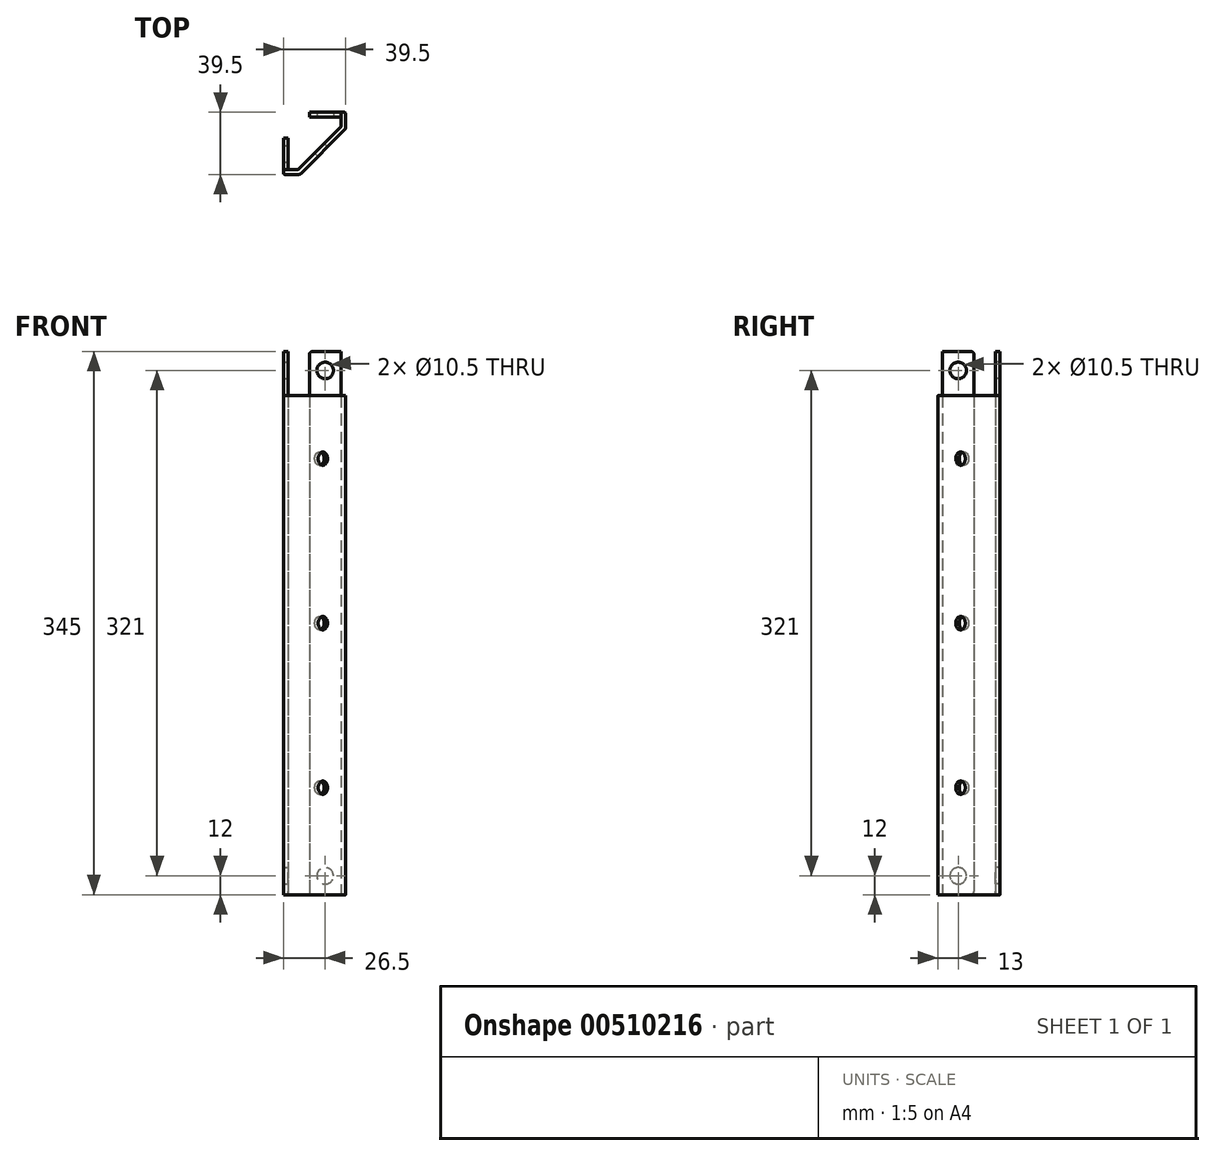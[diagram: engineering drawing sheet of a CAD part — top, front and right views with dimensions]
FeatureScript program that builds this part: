
annotation { "Feature Type Name" : "Feature", "Feature Type Description" : "" }
export const myFeature = defineFeature(function(context is Context, id is Id, definition is map)
    precondition{}
    {
        {
            var Q0;
            Q0=qCreatedBy(makeId("Top.planeOp"),FACE);
            var sketch = newSketch(context, id + "F0", { "sketchPlane" : qUnion([Q0])});
            skLineSegment(sketch, "E0", {"start": v(0, 53.87) * mm, "end": v(0, -58.58) * mm, "construction": true});
            skLineSegment(sketch, "E1", {"start": v(-55.23, 0) * mm, "end": v(53.75, 0) * mm, "construction": true});
            skLineSegment(sketch, "E2.bottom", {"start": v(-19.75, 19.75) * mm, "end": v(19.75, 19.75) * mm, "construction": true});
            skLineSegment(sketch, "E2.top", {"start": v(-19.75, -19.75) * mm, "end": v(19.75, -19.75) * mm, "construction": true});
            skLineSegment(sketch, "E2.left", {"start": v(-19.75, 19.75) * mm, "end": v(-19.75, -19.75) * mm, "construction": true});
            skLineSegment(sketch, "E2.right", {"start": v(19.75, 19.75) * mm, "end": v(19.75, -19.75) * mm, "construction": true});
            skLineSegment(sketch, "E3", {"start": v(-19.75, -19.75) * mm, "end": v(-19.75, 3.25) * mm});
            skLineSegment(sketch, "E4", {"start": v(-19.75, 3.25) * mm, "end": v(-16.75, 3.25) * mm});
            skLineSegment(sketch, "E5", {"start": v(-16.75, 3.25) * mm, "end": v(-16.75, -16.75) * mm});
            skLineSegment(sketch, "E6", {"start": v(-19.75, -19.75) * mm, "end": v(-9.25, -19.75) * mm});
            skLineSegment(sketch, "E7", {"start": v(-9.25, -19.75) * mm, "end": v(19.75, 9.25) * mm, "construction": true});
            skLineSegment(sketch, "E8", {"start": v(-16.75, -6.75) * mm, "end": v(-8.75, -6.75) * mm, "construction": true});
            skLineSegment(sketch, "E9", {"start": v(-8.75, -6.75) * mm, "end": v(-8.75, -15.25) * mm, "construction": true});
            skLineSegment(sketch, "E10.0", {"start": v(-10.5, -16.75) * mm, "end": v(16.75, 10.5) * mm});
            skLineSegment(sketch, "E11", {"start": v(-16.75, -16.75) * mm, "end": v(-10.5, -16.75) * mm});
            skLineSegment(sketch, "E12.0", {"start": v(-10.66, -18.34) * mm, "end": v(18.84, 11.16) * mm, "construction": true});
            skLineSegment(sketch, "E13", {"start": v(-9.25, -19.75) * mm, "end": v(19.75, 9.25) * mm});
            skLineSegment(sketch, "E14", {"start": v(19.75, 9.25) * mm, "end": v(19.75, 19.75) * mm});
            skLineSegment(sketch, "E15", {"start": v(19.75, 19.75) * mm, "end": v(-3.25, 19.75) * mm});
            skLineSegment(sketch, "E16", {"start": v(-3.25, 19.75) * mm, "end": v(-3.25, 16.75) * mm});
            skLineSegment(sketch, "E17", {"start": v(-3.25, 16.75) * mm, "end": v(16.75, 16.75) * mm});
            skLineSegment(sketch, "E18", {"start": v(16.75, 16.75) * mm, "end": v(16.75, 10.5) * mm});
            skSolve(sketch);
        }
        {
            var Q0;
            Q0=qSketchRegion(id+"F0",true);
            extrude(context, id + "F1", {"entities" : qUnion([Q0]), "depth" : 345 * mm, "symmetric" : true});
        }
        {
            var Q0;
            Q0=makeQuery(id+"F1.opExtrude","CAP_FACE",FACE,{"disambiguationData":[OSD([sQuery(id+"F0.wireOp",EDGE,"E3"),sQuery(id+"F0.wireOp",EDGE,"E4"),sQuery(id+"F0.wireOp",EDGE,"E5"),sQuery(id+"F0.wireOp",EDGE,"E6"),sQuery(id+"F0.wireOp",EDGE,"E10.0"),sQuery(id+"F0.wireOp",EDGE,"E11"),sQuery(id+"F0.wireOp",EDGE,"E13"),sQuery(id+"F0.wireOp",EDGE,"E14"),sQuery(id+"F0.wireOp",EDGE,"E15"),sQuery(id+"F0.wireOp",EDGE,"E16"),sQuery(id+"F0.wireOp",EDGE,"E17"),sQuery(id+"F0.wireOp",EDGE,"E18")])],"isStart":false});
            var sketch = newSketch(context, id + "F2", { "sketchPlane" : qUnion([Q0])});
            skLineSegment(sketch, "E19.0", {"start": v(-16.75, -16.75) * mm, "end": v(-10.5, -16.75) * mm});
            skLineSegment(sketch, "E19.1", {"start": v(-10.5, -16.75) * mm, "end": v(16.75, 10.5) * mm});
            skLineSegment(sketch, "E19.2", {"start": v(16.75, 16.75) * mm, "end": v(16.75, 10.5) * mm});
            skLineSegment(sketch, "E19.3", {"start": v(19.75, 9.25) * mm, "end": v(19.75, 19.75) * mm});
            skLineSegment(sketch, "E19.4", {"start": v(-9.25, -19.75) * mm, "end": v(19.75, 9.25) * mm});
            skLineSegment(sketch, "E19.5", {"start": v(-19.75, -19.75) * mm, "end": v(-9.25, -19.75) * mm});
            skLineSegment(sketch, "E20", {"start": v(-16.75, -16.75) * mm, "end": v(-19.75, -16.75) * mm});
            skLineSegment(sketch, "E21", {"start": v(-19.75, -16.75) * mm, "end": v(-19.75, -19.75) * mm});
            skLineSegment(sketch, "E22", {"start": v(16.75, 16.75) * mm, "end": v(16.75, 19.75) * mm});
            skLineSegment(sketch, "E23", {"start": v(16.75, 19.75) * mm, "end": v(19.75, 19.75) * mm});
            skSolve(sketch);
        }
        {
            var Q0;
            Q0=qSketchRegion(id+"F2",true);
            extrude(context, id + "F3", {"entities" : qUnion([Q0]), "operationType" : NewBodyOperationType.REMOVE, "oppositeDirection" : true, "depth" : 28 * mm});
        }
        {
            var Q0;
            Q0=makeQuery(id+"F1.opExtrude","SWEPT_FACE",FACE,{"disambiguationData":[OSD([sQuery(id+"F0.wireOp",EDGE,"E13")])]});
            var sketch = newSketch(context, id + "F4", { "sketchPlane" : qUnion([Q0])});
            skLineSegment(sketch, "E24", {"start": v(0, 144.5) * mm, "end": v(0, -144.5) * mm, "construction": true});
            skLineSegment(sketch, "E25", {"start": v(-20.5, 0) * mm, "end": v(20.5, 0) * mm, "construction": true});
            skCircle(sketch, "E26", {"center": v(0, 104.5) * mm, "radius": 4.25 * mm});
            skCircle(sketch, "E27.MirrorC", {"center": v(0, -104.5) * mm, "radius": 4.25 * mm});
            skCircle(sketch, "E28", {"center": v(0, 0) * mm, "radius": 4.25 * mm});
            skSolve(sketch);
        }
        {
            var Q0;
            Q0=qSketchRegion(id+"F4",true);
            extrude(context, id + "F5", {"entities" : qUnion([Q0]), "operationType" : NewBodyOperationType.REMOVE, "oppositeDirection" : true, "depth" : 25 * mm});
        }
        {
            var Q0;
            Q0=makeQuery(id+"F1.opExtrude","SWEPT_FACE",FACE,{"disambiguationData":[OSD([sQuery(id+"F0.wireOp",EDGE,"E5")])]});
            var sketch = newSketch(context, id + "F6", { "sketchPlane" : qUnion([Q0])});
            skLineSegment(sketch, "E29", {"start": v(-6.75, 172.5) * mm, "end": v(-6.75, -172.5) * mm, "construction": true});
            skCircle(sketch, "E30", {"center": v(-6.75, 160.5) * mm, "radius": 5.25 * mm});
            skCircle(sketch, "E31", {"center": v(-6.75, -160.5) * mm, "radius": 5.25 * mm});
            skSolve(sketch);
        }
        {
            var Q0;
            Q0=qSketchRegion(id+"F6",true);
            extrude(context, id + "F7", {"entities" : qUnion([Q0]), "operationType" : NewBodyOperationType.REMOVE, "oppositeDirection" : true, "depth" : 25 * mm});
        }
        {
            var Q0;
            Q0=makeQuery(id+"F1.opExtrude","SWEPT_FACE",FACE,{"disambiguationData":[OSD([sQuery(id+"F0.wireOp",EDGE,"E17")])]});
            var sketch = newSketch(context, id + "F8", { "sketchPlane" : qUnion([Q0])});
            skLineSegment(sketch, "E32", {"start": v(6.75, 172.5) * mm, "end": v(6.75, -172.5) * mm, "construction": true});
            skCircle(sketch, "E33", {"center": v(6.75, 160.5) * mm, "radius": 5.25 * mm});
            skCircle(sketch, "E34", {"center": v(6.75, -160.5) * mm, "radius": 5.25 * mm});
            skSolve(sketch);
        }
        {
            var Q0;
            Q0=qSketchRegion(id+"F8",true);
            extrude(context, id + "F9", {"entities" : qUnion([Q0]), "operationType" : NewBodyOperationType.REMOVE, "oppositeDirection" : true, "depth" : 25 * mm});
        }
        {
            var Q0;
            Q0=makeQuery(id+"F1.opExtrude","SWEPT_EDGE",EDGE,{"disambiguationData":[OSD([sQuery(id+"F0.wireOp",EDGE,"E6"),sQuery(id+"F0.wireOp",EDGE,"E13")])]});
            var Q1;
            Q1=makeQuery(id+"F1.opExtrude","SWEPT_EDGE",EDGE,{"disambiguationData":[OSD([sQuery(id+"F0.wireOp",EDGE,"E13"),sQuery(id+"F0.wireOp",EDGE,"E14")])]});
            var Q2;
            Q2=makeQuery(id+"F3.boolean.opBoolean","COPY",EDGE,{"derivedFrom":makeQuery(id+"F3.opExtrude","CAP_EDGE",EDGE,{"disambiguationData":[OSD([sQuery(id+"F2.wireOp",EDGE,"E19.2"),sQuery(id+"F2.wireOp",EDGE,"E22")])],"isStart":true})});
            var Q3;
            Q3=makeQuery(id+"F1.opExtrude","CAP_EDGE",EDGE,{"disambiguationData":[OSD([sQuery(id+"F0.wireOp",EDGE,"E16")])],"isStart":false});
            var Q4;
            Q4=makeQuery(id+"F1.opExtrude","CAP_EDGE",EDGE,{"disambiguationData":[OSD([sQuery(id+"F0.wireOp",EDGE,"E4")])],"isStart":false});
            var Q5;
            Q5=makeQuery(id+"F3.boolean.opBoolean","COPY",EDGE,{"derivedFrom":makeQuery(id+"F3.opExtrude","CAP_EDGE",EDGE,{"disambiguationData":[OSD([sQuery(id+"F2.wireOp",EDGE,"E19.0"),sQuery(id+"F2.wireOp",EDGE,"E20")])],"isStart":true})});
            var Q6;
            Q6=makeQuery(id+"Fec6EYU1eJzkxKK_1.1.F3.boolean.opBoolean","COPY",EDGE,{"derivedFrom":makeQuery(id+"Fec6EYU1eJzkxKK_1.1.F3.opExtrude","CAP_EDGE",EDGE,{"disambiguationData":[OSD([sQuery(id+"F2.wireOp",EDGE,"E19.0"),sQuery(id+"F2.wireOp",EDGE,"E20")])],"isStart":true})});
            var Q7;
            Q7=makeQuery(id+"F1.opExtrude","CAP_EDGE",EDGE,{"disambiguationData":[OSD([sQuery(id+"F0.wireOp",EDGE,"E4")])],"isStart":true});
            var Q8;
            Q8=makeQuery(id+"F1.opExtrude","CAP_EDGE",EDGE,{"disambiguationData":[OSD([sQuery(id+"F0.wireOp",EDGE,"E16")])],"isStart":true});
            var Q9;
            Q9=makeQuery(id+"Fec6EYU1eJzkxKK_1.1.F3.boolean.opBoolean","COPY",EDGE,{"derivedFrom":makeQuery(id+"Fec6EYU1eJzkxKK_1.1.F3.opExtrude","CAP_EDGE",EDGE,{"disambiguationData":[OSD([sQuery(id+"F2.wireOp",EDGE,"E19.2"),sQuery(id+"F2.wireOp",EDGE,"E22")])],"isStart":true})});
            fillet(context, id + "F10", {"entities" : qUnion([Q0, Q1, Q2, Q3, Q4, Q5, Q6, Q7, Q8, Q9]), "radius" : 2 * mm, "tangentPropagation" : true, "allowEdgeOverflow" : false});
        }
        {
            var Q0;
            Q0=makeQuery(id+"F1.opExtrude","SWEPT_EDGE",EDGE,{"disambiguationData":[OSD([sQuery(id+"F0.wireOp",EDGE,"E10.0"),sQuery(id+"F0.wireOp",EDGE,"E11")])]});
            var Q1;
            Q1=makeQuery(id+"F1.opExtrude","SWEPT_EDGE",EDGE,{"disambiguationData":[OSD([sQuery(id+"F0.wireOp",EDGE,"E10.0"),sQuery(id+"F0.wireOp",EDGE,"E18")])]});
            fillet(context, id + "F11", {"entities" : qUnion([Q0, Q1]), "radius" : 0.5 * mm, "tangentPropagation" : true, "allowEdgeOverflow" : false});
        }
        {
            var Q0;
            Q0=makeQuery(id+"F1.opExtrude","SWEPT_EDGE",EDGE,{"disambiguationData":[OSD([sQuery(id+"F0.wireOp",EDGE,"E3"),sQuery(id+"F0.wireOp",EDGE,"E6")])]});
            var Q1;
            Q1=makeQuery(id+"F1.opExtrude","SWEPT_EDGE",EDGE,{"disambiguationData":[OSD([sQuery(id+"F0.wireOp",EDGE,"E14"),sQuery(id+"F0.wireOp",EDGE,"E15")])]});
            fillet(context, id + "F12", {"entities" : qUnion([Q0, Q1]), "radius" : 1 * mm, "tangentPropagation" : true, "allowEdgeOverflow" : false});
        }
    });
